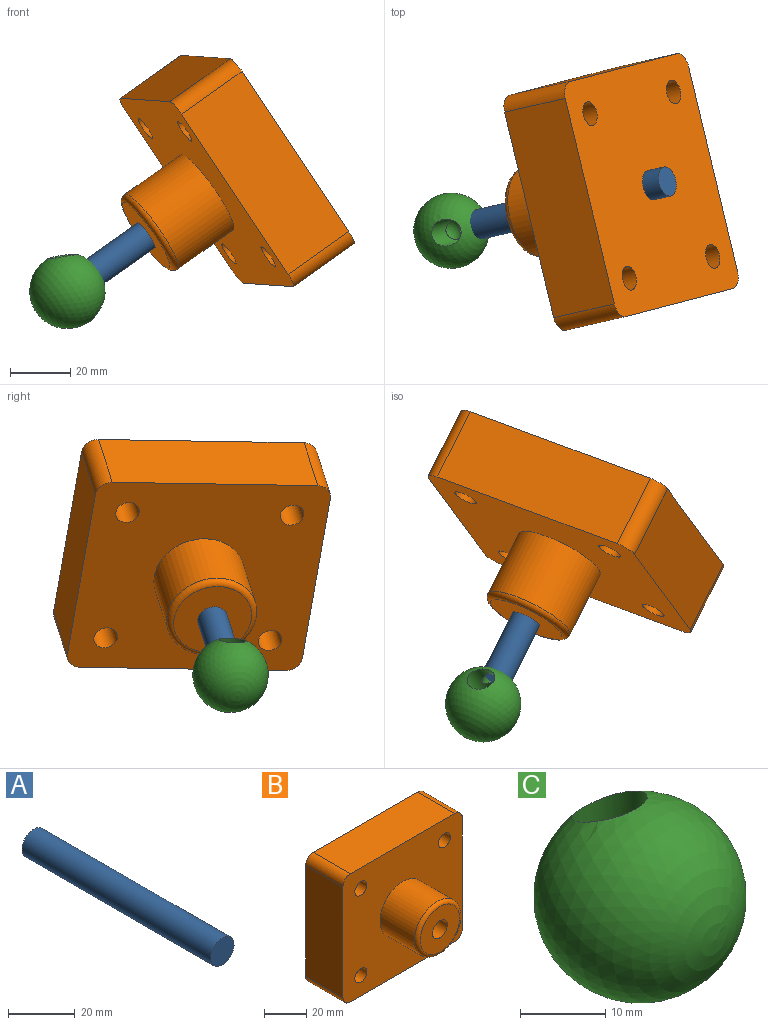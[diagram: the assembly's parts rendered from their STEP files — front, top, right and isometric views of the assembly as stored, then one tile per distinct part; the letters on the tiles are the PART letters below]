
ASSEMBLY  parts=3 mates=5
PART A: 3 faces, bbox 9.9x80x9.9 mm
  f0: plane 9.88x9.88mm, normal (0,1,0), area 76.7mm2, adj f1
  f1: cylinder r=4.94mm len=80mm, axis (0,1,0), area 2483.1mm2, adj f0,f2
  f2: plane 9.88x9.88mm, normal (0,-1,0), area 76.7mm2, adj f1
PART B: 18 faces, bbox 80x50x74.4 mm
  f0: plane 70x25mm, normal (0,0,1), area 1750mm2, adj f8,f9,f13,f16
  f1: plane 64.4x25mm, normal (-1,0,0), area 1610mm2, adj f8,f9,f13,f14
  f2: plane 70x25mm, normal (0,0,-1), area 1750mm2, adj f8,f9,f14,f15
  f3: cylinder r=4mm len=25mm, axis (0,1,0), area 628.3mm2, adj f8,f9
  f4: cylinder r=4mm len=25mm, axis (0,1,0), area 628.3mm2, adj f8,f9
  f5: cylinder r=4mm len=25mm, axis (0,1,0), area 628.3mm2, adj f8,f9
  f6: cylinder r=4mm len=25mm, axis (0,1,0), area 628.3mm2, adj f8,f9
  f7: plane 64.4x25mm, normal (1,0,0), area 1610mm2, adj f8,f9,f15,f16
  f8: plane 80x74.4mm, normal (0,-1,0), area 5008.3mm2, adj f0,f1,f2,f3,f4,f5,f6,f7
  f9: plane 80x74.4mm, normal (0,1,0), area 5651mm2, adj f0,f1,f2,f3,f4,f5,f6,f7
  f10: cylinder r=5mm len=50mm, axis (0,1,0), area 1570.8mm2, adj f9,f12
  f11: cylinder r=15.15mm len=30.3mm, axis (0,1,0), area 2189.6mm2, adj f8,f17
  f12: plane 26.3x26.3mm, normal (0,-1,0), area 464.8mm2, adj f10,f17
  f13: cylinder r=5mm len=25mm, axis (0,-1,0), area 196.3mm2, adj f0,f1,f8,f9
  f14: cylinder r=5mm len=25mm, axis (0,1,0), area 196.3mm2, adj f1,f2,f8,f9
  f15: cylinder r=5mm len=25mm, axis (0,-1,0), area 196.3mm2, adj f2,f7,f8,f9
  f16: cylinder r=5mm len=25mm, axis (0,1,0), area 196.3mm2, adj f0,f7,f8,f9
  f17: torus R=13.15mm, axis (0,-1,0), area 284.7mm2, adj f11,f12
PART C: 5 faces, bbox 25x24.2x25 mm
  f0: sphere r=4mm, area 134.9mm2, adj f1
  f1: cylinder r=4.45mm len=24.98mm, axis (0,0,-1), area 478.9mm2, adj f0,f2,f3
  f2: cylinder r=4mm len=8mm, axis (0,-1,0), area 75.6mm2, adj f1,f4
  f3: sphere r=12.5mm, area 1754.4mm2, adj f1,f4
  f4: cone r=4.49mm half-angle=55.5deg, axis (0,1,0), area 15.8mm2, adj f2,f3
PLACE A rot(axis=(0.6,0.76,0.24),159.5deg) t=(113.18,-295.97,91.45)mm
PLACE B rot(axis=(0.6,0.76,0.24),159.5deg) t=(115.01,-186.96,111.77)mm
PLACE C rot(axis=(0.6,0.76,0.24),159.5deg) t=(36.61,-270.21,44.91)mm
MATE slider B.f10 <-> A.f1  axis (-0.8,-0.18,-0.57) through (74.86,-196.07,83.4)mm
MATE slider A.f1 <-> C.f2  axis (-0.8,-0.18,-0.57) through (56.05,-200.34,70.11)mm
MATE slider B.f10 <-> A.f1  axis (0.8,0.18,0.57) through (94.94,-191.51,97.59)mm
MATE slider C.f2 <-> A.f1  axis (-0.8,-0.18,-0.57) through (56.05,-200.34,70.11)mm
MATE planar A.f1 <-> C.f2  axis (-0.8,-0.18,-0.57) through (56.05,-200.34,70.11)mm
